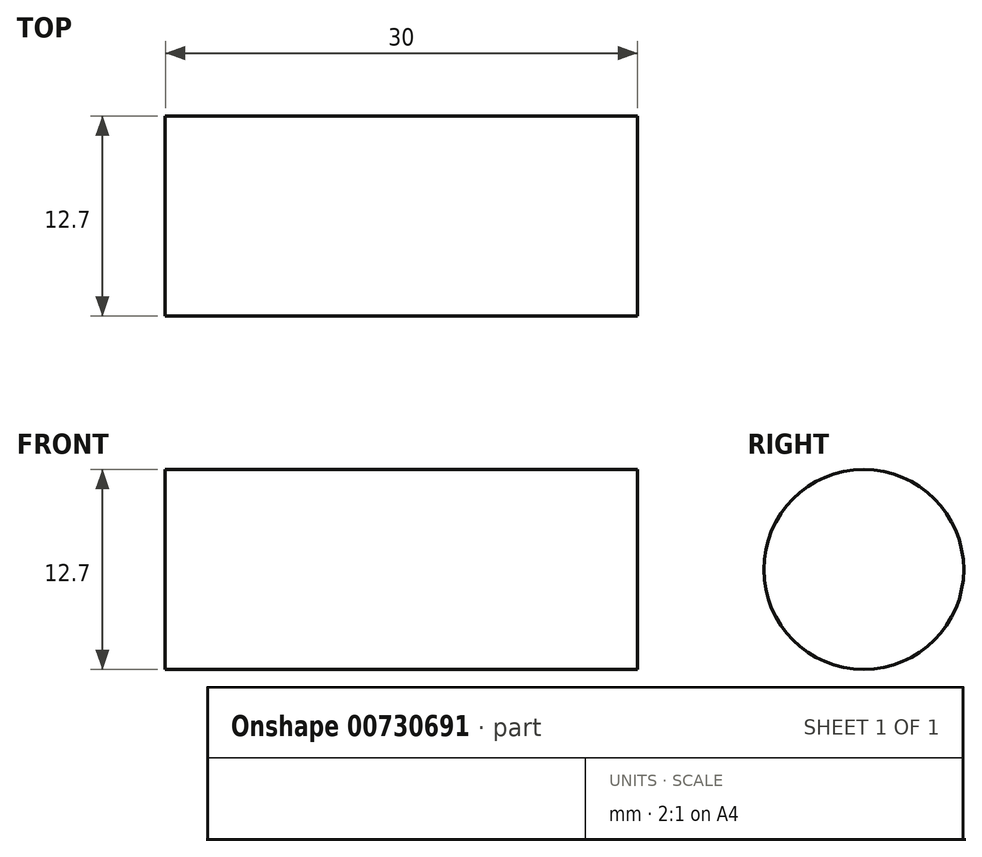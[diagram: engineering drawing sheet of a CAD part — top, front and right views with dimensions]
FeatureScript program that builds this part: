
annotation { "Feature Type Name" : "Feature", "Feature Type Description" : "" }
export const myFeature = defineFeature(function(context is Context, id is Id, definition is map)
    precondition{}
    {
        {
            var Q0;
            Q0=qCreatedBy(makeId("Top.planeOp"),FACE);
            var sketch = newSketch(context, id + "F0", { "sketchPlane" : qUnion([Q0])});
            skLineSegment(sketch, "E0.bottom", {"start": v(-23.92, 1) * mm, "end": v(6.08, 1) * mm});
            skLineSegment(sketch, "E0.top", {"start": v(-23.92, -5.36) * mm, "end": v(6.08, -5.36) * mm});
            skLineSegment(sketch, "E0.left", {"start": v(-23.92, 1) * mm, "end": v(-23.92, -5.36) * mm});
            skLineSegment(sketch, "E0.right", {"start": v(6.08, 1) * mm, "end": v(6.08, -5.36) * mm});
            skSolve(sketch);
        }
        {
            var Q0;
            Q0=makeQuery(id+"F0.imprint","IMPRINT",FACE,{"disambiguationData":[TD([[makeQuery(id+"F0.imprint","IMPRINT",EDGE,{"derivedFrom":sQuery(id+"F0.wireOp",EDGE,"E0.bottom")}),-1.0]])]});
            var Q1;
            Q1=sQuery(id+"F0.wireOp",EDGE,"E0.bottom");
            revolve(context, id + "F1", {"surfaceOperationType" : NewSurfaceOperationType.NEW, "entities" : qUnion([Q0]), "axis" : qUnion([Q1]), "revolveType" : RevolveType.FULL});
        }
    });
